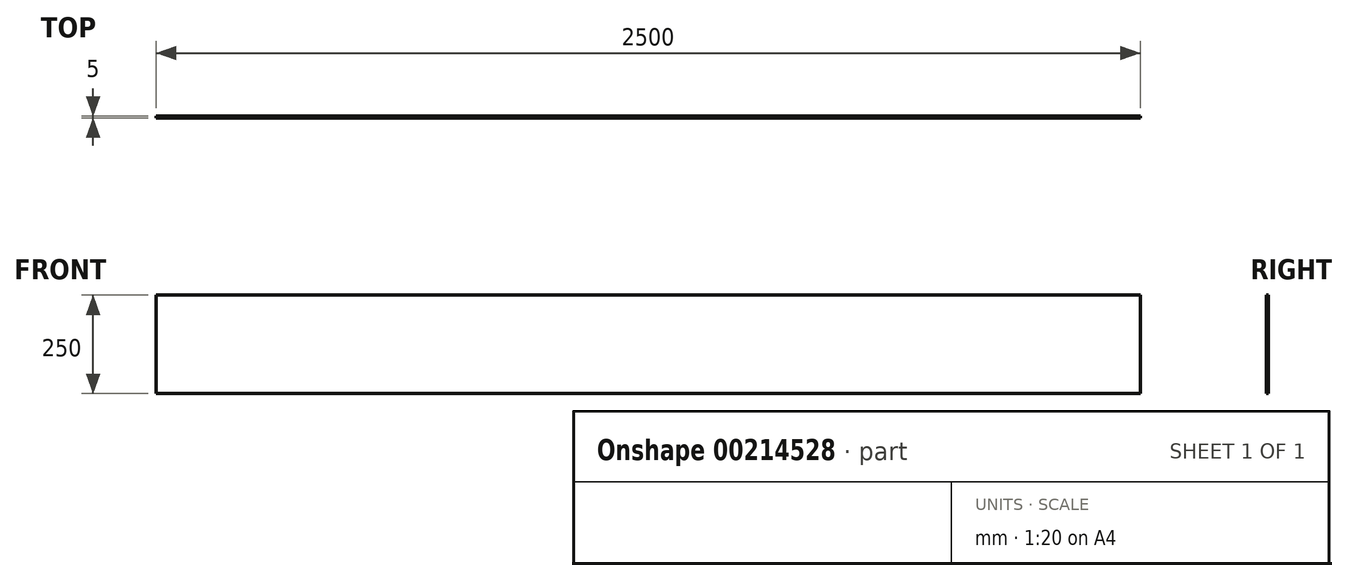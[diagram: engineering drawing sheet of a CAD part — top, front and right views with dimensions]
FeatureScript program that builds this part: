
annotation { "Feature Type Name" : "Feature", "Feature Type Description" : "" }
export const myFeature = defineFeature(function(context is Context, id is Id, definition is map)
    precondition{}
    {
        {
            var Q0;
            Q0=qCreatedBy(makeId("Front.planeOp"),FACE);
            var sketch = newSketch(context, id + "F0", { "sketchPlane" : qUnion([Q0])});
            skLineSegment(sketch, "E0.bottom", {"start": v(-1250, 125) * mm, "end": v(1250, 125) * mm});
            skLineSegment(sketch, "E0.top", {"start": v(-1250, -125) * mm, "end": v(1250, -125) * mm});
            skLineSegment(sketch, "E0.left", {"start": v(-1250, 125) * mm, "end": v(-1250, -125) * mm});
            skLineSegment(sketch, "E0.right", {"start": v(1250, 125) * mm, "end": v(1250, -125) * mm});
            skSolve(sketch);
        }
        {
            var Q0;
            Q0 = qSketchRegion(id + "F0", true);
            extrude(context, id + "F1", {"entities" : qUnion([Q0]), "depth" : 5 * mm});
        }
    });
